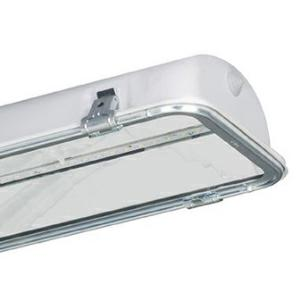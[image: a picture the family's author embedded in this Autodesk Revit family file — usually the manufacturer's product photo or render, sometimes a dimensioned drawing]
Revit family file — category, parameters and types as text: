
# Revit family: 3f_filippi_-_beta_i3f_76_vt_concentrato_3f_filippi_-_55666_-_i3f_led_762x30w_conc_vt_l1565
name_source: partatom
category: Lighting Fixtures
units: mm (PartAtom-declared; Revit-internal decimal feet)

## family parameters
Cut with Voids When Loaded = No
Host = Face
Light Source = No
Part Type = Normal
Room Calculation Point = No
Round Connector Dimension = Use Diameter
Shared = No

## types (1)
- 3F Filippi - Beta i3F 76 VT Concentrato (1 x LED, 9823 lm, 66 W, 4000 K)
    Apparent Load = 66 VA
    Approval mark = ENEC
    CIE Flux Codes = 59 91 99 100 100
    Color Rendering = 80
    Color Temperature = 4000 K
    Control Gear = Electronic ballast
    Default Elevation = 1800 mm
    Description = ILLUMINOTECHNICAL
Luminous efficiency 100% (DLOR 100%, ULOR 0%).
Initial luminous flux of the luminaire 9823 lm.
Concentrated elliptical distribution.
Installation Interdistance Transv.D = 0.74 x hu - Long.D = 1.25 x hu.
Tabular UGR (CIE 117 - 4H-8H; S=0.25H; 70/50/20): RUG 18.4 - 24.2.
Beam angle: 65° - 109°.
Luminous efficacy 149 lm/W.
Lifetime (L93/B10): 30000 h. (tq+25°C)
Lifetime (L90/B10): 50000 h. (tq+25°C)
Lifetime (L85/B10): 80000 h. (tq+25°C)
Lifetime (L80/B10): 100000 h. (tq+25°C)
Lifetime (L85/B10): 50000 h. (tq+35°C)
Sudden decreased luminous flux after 50000 hours: 0% (C0).
Photobiological safety in compliance with IEC/TR 62778: RG0 risk exempt, (IEC 62471).
In compliance with IEC/EN 62722-2-1 - IEC/EN 62717 standards.

SOURCE
2 linear LED modules 30W/840.
Energy efficiency class (UE 2019/2020 - UE 2019/2015): D.
CIE 13.3 Colour rendering index: CRI >80 (R9 <50%).
IES TM-30 Fidelity Index: Rf = 84 Rg = 95.
CCT nominal colour temperature 4000 K.
Colour initial tolerance (MacAdam): SDCM 3.

MECHANICAL
Single-piece housing in pressed steel, powder-coated in white epoxy-polyester.
Transparent glass, non-combustible, tempered, mounted and locked to the single-piece galvanised steel perimetrical frame, sealing gasket, hinged opening by means of galvanised steel clips.
Concentrated flow recuperator, oversized, in specular aluminium with superficial titanium-magnesium treatment, non-iridescent.
Gear-tray unit in hot-galvanised steel, painted in white polyester, fixed to the housing by means of "Ribloc" rapid devices in galvanised steel, hinged opening.
Luminaire with limited surface temperature. - D - (EN 60598-2-24)
Dimensions: 1565x235 mm, height 105 mm. Weight 9.885 kg.
IP65 protection degree.
Mechanical strength to impacts IK09 (10 joule).
Glow-wire test resistance 960°C.

ELECTRICAL
Halogen Free electronic wiring 230V-50/60Hz, power factor 0.97, THD <25%, constant output current, SELV, class I, 1 driver.
Power of the luminaire 66 W.
CE - IEC 60598-1 - EN 60598-1.
SAFE FLICKER: PstLM=<1 and SVM=<0.4 (IEC TR 61547-1 and IEC TR 63158), to ensure a more comfortable and safe light.
Luminaire compliant with EN 60598-2-22 for power supply from a centralised emergency system CPSS (Central Power Supply System), not incorporated in the luminaire - high risk areas excluded. The default power and flux are 100% in AC and 100% in DC.
Ambient temperature from -20°C to +35°C.
Temperature class T6 max 85°C.
Relative humidity UR: <85%.

INSTALLATION
Ceiling / Suspended / Wall.
All accessories dedicated to this product are available on the Catalog and on our website www.3F-Filippi.com.

APPLICATIONS
In industrial environments, stores and dry, dusty indoor environments, subject to occasional water splashes.

WARNING
Fixture not suitable for cold stores with an ambient temperature <0°C and/or relative humidity >85%.
Luminaire designed for disposal/recycling at end-of-life.
Replaceable (LED only) light source by a professional. Replaceable control gear by a professional.
    Height = 105 mm
    Lamp = 1 x LED
    Lamp Light Flux = 9823 lm
    Lamp Power = 66 W
    Lamp count = 1
    Length = 1565 mm
    Lifetime = 50000 h
    Luminous efficacy = 149 lm/W
    Manufacturer = 3F Filippi
    ModVariant = No
    Model = 3F Filippi - 55666 - i3F LED 762x30W CONC VT L1565
    Mounting Place = Ceiling
    Mounting Type = Pendant
    Number of Poles = 1
    OnlyDefault = Yes
    Power Factor = 1
    Product Name = 3F Filippi - Beta i3F 76 VT Concentrato
    Product group = pendant luminaire
    ProductGroupID = 9
    Protection Class = Protection class I
    Protection Degree = IP 65
    RLX_Detail_Level = 1
    RLX_Emergency_Light_Flux = 0 lm
    RLX_Emergency_Type = 0
    RLX_Emergency_Type_DB = No
    RlxData = <blob elided: 70517 chars, md5=72293a64>
    Socket = socket
    Standby Power = 0 W
    System Light Flux = 9823 lm
    System Power = 66 W
    Type Comments = Product without accessories
    Type Image = 3ffilippi_55666.jpg
    URL = http://relux.com
    VarID = ---
    Voltage = 0 V
    Weight = 0.00 kg
    Width = 235 mm

## geometry (parser evidence)
native form markers: Blend x4, Sweep x10
no freeform markers — native parametric forms only
